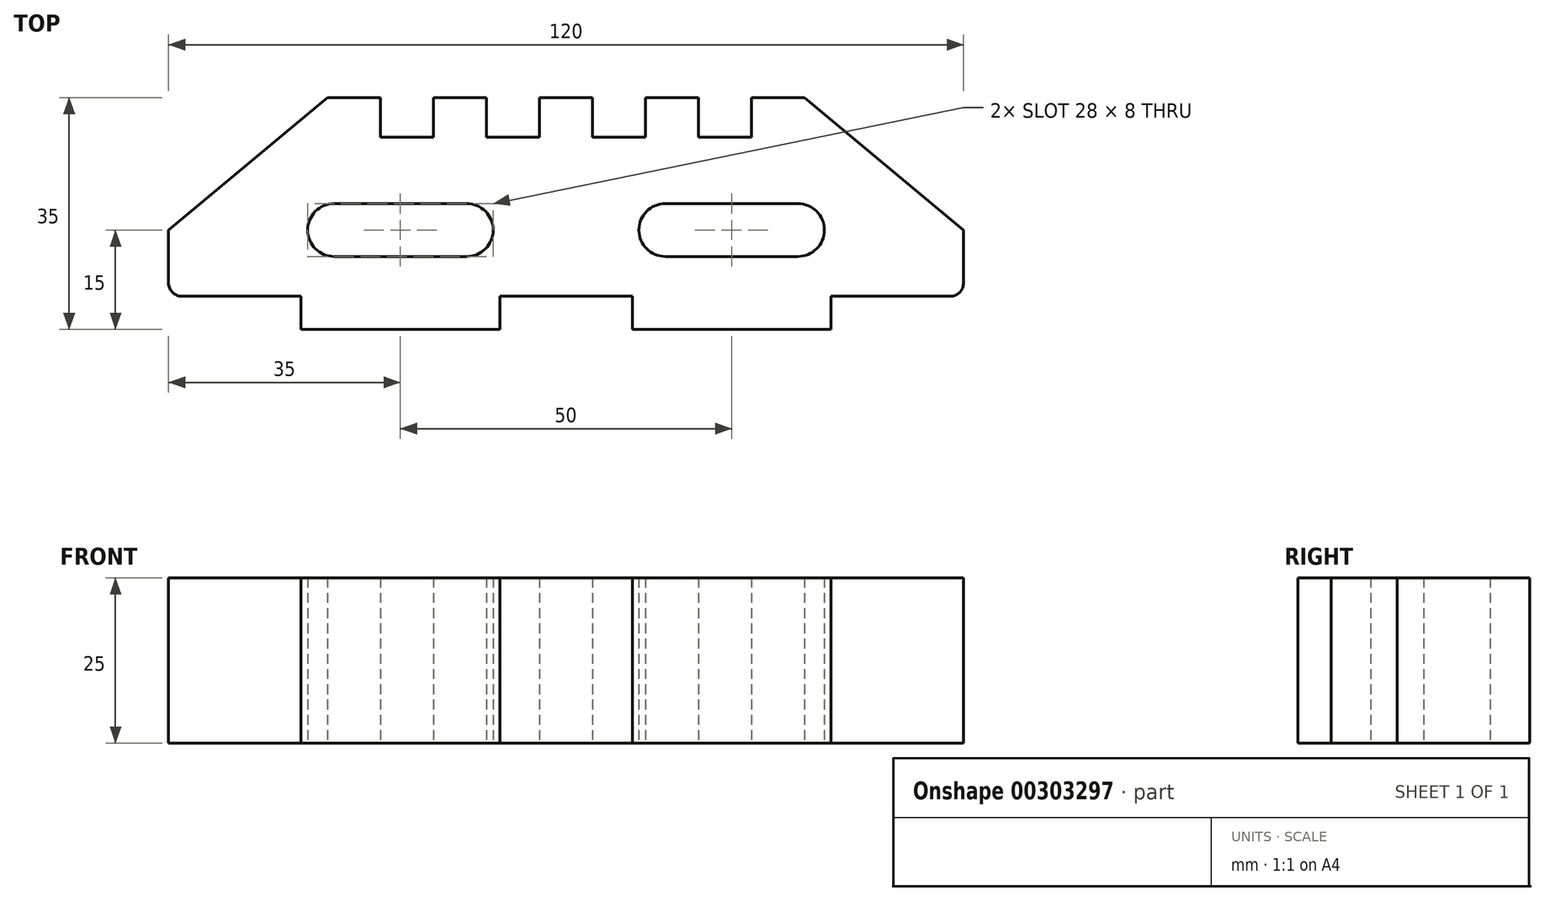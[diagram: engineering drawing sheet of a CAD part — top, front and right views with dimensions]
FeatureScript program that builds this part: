
annotation { "Feature Type Name" : "Feature", "Feature Type Description" : "" }
export const myFeature = defineFeature(function(context is Context, id is Id, definition is map)
    precondition{}
    {
        {
            var Q0;
            Q0=qCreatedBy(makeId("Top.planeOp"),FACE);
            var sketch = newSketch(context, id + "F0", { "sketchPlane" : qUnion([Q0])});
            skLineSegment(sketch, "E0", {"start": v(0, 0) * mm, "end": v(30, 0) * mm});
            skLineSegment(sketch, "E1", {"start": v(30, 0) * mm, "end": v(30, 5) * mm});
            skLineSegment(sketch, "E2", {"start": v(30, 5) * mm, "end": v(50, 5) * mm});
            skLineSegment(sketch, "E3", {"start": v(50, 5) * mm, "end": v(50, 0) * mm});
            skLineSegment(sketch, "E4", {"start": v(50, 0) * mm, "end": v(80, 0) * mm});
            skLineSegment(sketch, "E5", {"start": v(0, 0) * mm, "end": v(0, 5) * mm});
            skLineSegment(sketch, "E6", {"start": v(0, 5) * mm, "end": v(-18, 5) * mm});
            skLineSegment(sketch, "E7", {"start": v(80, 0) * mm, "end": v(80, 5) * mm});
            skLineSegment(sketch, "E8", {"start": v(80, 5) * mm, "end": v(98, 5) * mm});
            skLineSegment(sketch, "E9", {"start": v(-20, 7) * mm, "end": v(-20, 15) * mm});
            skLineSegment(sketch, "E10", {"start": v(4, 35) * mm, "end": v(-20, 15) * mm});
            skLineSegment(sketch, "E11", {"start": v(4, 35) * mm, "end": v(12, 35) * mm});
            skLineSegment(sketch, "E12", {"start": v(100, 7) * mm, "end": v(100, 15) * mm});
            skLineSegment(sketch, "E13", {"start": v(76, 35) * mm, "end": v(100, 15) * mm});
            skLineSegment(sketch, "E14", {"start": v(76, 35) * mm, "end": v(68, 35) * mm});
            skLineSegment(sketch, "E15", {"start": v(12, 35) * mm, "end": v(12, 29) * mm});
            skLineSegment(sketch, "E16", {"start": v(12, 29) * mm, "end": v(20, 29) * mm});
            skLineSegment(sketch, "E17", {"start": v(68, 29) * mm, "end": v(68, 35) * mm});
            skLineSegment(sketch, "E18", {"start": v(28, 29) * mm, "end": v(36, 29) * mm});
            skLineSegment(sketch, "E19", {"start": v(44, 29) * mm, "end": v(52, 29) * mm});
            skLineSegment(sketch, "E20", {"start": v(60, 29) * mm, "end": v(60, 35) * mm});
            skLineSegment(sketch, "E21", {"start": v(52, 35) * mm, "end": v(52, 29) * mm});
            skLineSegment(sketch, "E22", {"start": v(44, 29) * mm, "end": v(44, 35) * mm});
            skLineSegment(sketch, "E23", {"start": v(28, 29) * mm, "end": v(28, 35) * mm});
            skLineSegment(sketch, "E24", {"start": v(28, 35) * mm, "end": v(20, 35) * mm});
            skLineSegment(sketch, "E25", {"start": v(20, 35) * mm, "end": v(20, 29) * mm});
            skLineSegment(sketch, "E26", {"start": v(52, 35) * mm, "end": v(60, 35) * mm});
            skLineSegment(sketch, "E27.trimOffspring", {"start": v(60, 29) * mm, "end": v(68, 29) * mm});
            skLineSegment(sketch, "E28", {"start": v(-71.06, 63.02) * mm, "end": v(-69.55, 42.35) * mm});
            skLineSegment(sketch, "E29", {"start": v(-67.18, 40.53) * mm, "end": v(-46.46, 44.49) * mm});
            skPoint(sketch, "E30.visualSharp", {"position": v(-69.39, 40.11) * mm});
            skArc(sketch, "E30.filletArc", {"start": v(-69.55, 42.35) * mm, "mid": v(-68.78, 40.91) * mm, "end": v(-67.18, 40.53) * mm});
            skPoint(sketch, "E31.visualSharp", {"position": v(-20, 5) * mm});
            skArc(sketch, "E31.filletArc", {"start": v(-20, 7) * mm, "mid": v(-19.41, 5.59) * mm, "end": v(-18, 5) * mm});
            skPoint(sketch, "E32.visualSharp", {"position": v(100, 5) * mm});
            skArc(sketch, "E32.filletArc", {"start": v(98, 5) * mm, "mid": v(99.41, 5.59) * mm, "end": v(100, 7) * mm});
            skLineSegment(sketch, "E33", {"start": v(30, 5) * mm, "end": v(40, 5) * mm, "construction": true});
            skLineSegment(sketch, "E34", {"start": v(40, 5) * mm, "end": v(40, 35) * mm, "construction": true});
            skLineSegment(sketch, "E35", {"start": v(36, 29) * mm, "end": v(36, 35) * mm});
            skLineSegment(sketch, "E36", {"start": v(36, 35) * mm, "end": v(44, 35) * mm});
            skLineSegment(sketch, "E37", {"start": v(-20, 15) * mm, "end": v(100, 15) * mm, "construction": true});
            skLineSegment(sketch, "E38", {"start": v(40, 21.27) * mm, "end": v(51, 21.27) * mm, "construction": true});
            skLineSegment(sketch, "E39", {"start": v(50, 0) * mm, "end": v(51, 0) * mm, "construction": true});
            skLineSegment(sketch, "E40", {"start": v(51, 0) * mm, "end": v(51, 15) * mm, "construction": true});
            skLineSegment(sketch, "E41", {"start": v(51, 15) * mm, "end": v(51, 15) * mm});
            skLineSegment(sketch, "E42", {"start": v(51, 15) * mm, "end": v(79, 15) * mm});
            skLineSegment(sketch, "E43", {"start": v(79, 15) * mm, "end": v(79, 15) * mm});
            skLineSegment(sketch, "E44", {"start": v(75, 11) * mm, "end": v(55, 11) * mm});
            skLineSegment(sketch, "E45", {"start": v(55, 19) * mm, "end": v(75, 19) * mm});
            skPoint(sketch, "E46.visualSharp", {"position": v(79, 19) * mm});
            skArc(sketch, "E46.filletArc", {"start": v(79, 15) * mm, "mid": v(77.83, 17.83) * mm, "end": v(75, 19) * mm});
            skPoint(sketch, "E47.visualSharp", {"position": v(79, 11) * mm});
            skArc(sketch, "E47.filletArc", {"start": v(75, 11) * mm, "mid": v(77.83, 12.17) * mm, "end": v(79, 15) * mm});
            skPoint(sketch, "E48.visualSharp", {"position": v(51, 11) * mm});
            skArc(sketch, "E48.filletArc", {"start": v(51, 15) * mm, "mid": v(52.17, 12.17) * mm, "end": v(55, 11) * mm});
            skPoint(sketch, "E49.visualSharp", {"position": v(51, 19) * mm});
            skArc(sketch, "E49.filletArc", {"start": v(55, 19) * mm, "mid": v(52.17, 17.83) * mm, "end": v(51, 15) * mm});
            skLineSegment(sketch, "E50", {"start": v(30, 0) * mm, "end": v(29, 0) * mm});
            skLineSegment(sketch, "E51", {"start": v(29, 15) * mm, "end": v(29, 15) * mm});
            skLineSegment(sketch, "E52", {"start": v(25, 11) * mm, "end": v(5, 11) * mm});
            skLineSegment(sketch, "E53", {"start": v(1, 15) * mm, "end": v(1, 15) * mm});
            skLineSegment(sketch, "E54", {"start": v(5, 19) * mm, "end": v(25, 19) * mm});
            skPoint(sketch, "E55.visualSharp", {"position": v(1, 19) * mm});
            skArc(sketch, "E55.filletArc", {"start": v(5, 19) * mm, "mid": v(2.17, 17.83) * mm, "end": v(1, 15) * mm});
            skPoint(sketch, "E56.visualSharp", {"position": v(29, 19) * mm});
            skArc(sketch, "E56.filletArc", {"start": v(29, 15) * mm, "mid": v(27.83, 17.83) * mm, "end": v(25, 19) * mm});
            skPoint(sketch, "E57.visualSharp", {"position": v(29, 11) * mm});
            skArc(sketch, "E57.filletArc", {"start": v(25, 11) * mm, "mid": v(27.83, 12.17) * mm, "end": v(29, 15) * mm});
            skPoint(sketch, "E58.visualSharp", {"position": v(1, 11) * mm});
            skArc(sketch, "E58.filletArc", {"start": v(1, 15) * mm, "mid": v(2.17, 12.17) * mm, "end": v(5, 11) * mm});
            skSolve(sketch);
        }
        {
            var Q0;
            Q0 = qSketchRegion(id + "F0", true);
            extrude(context, id + "F1", {"entities" : qUnion([Q0]), "depth" : 25 * mm});
        }
    });
